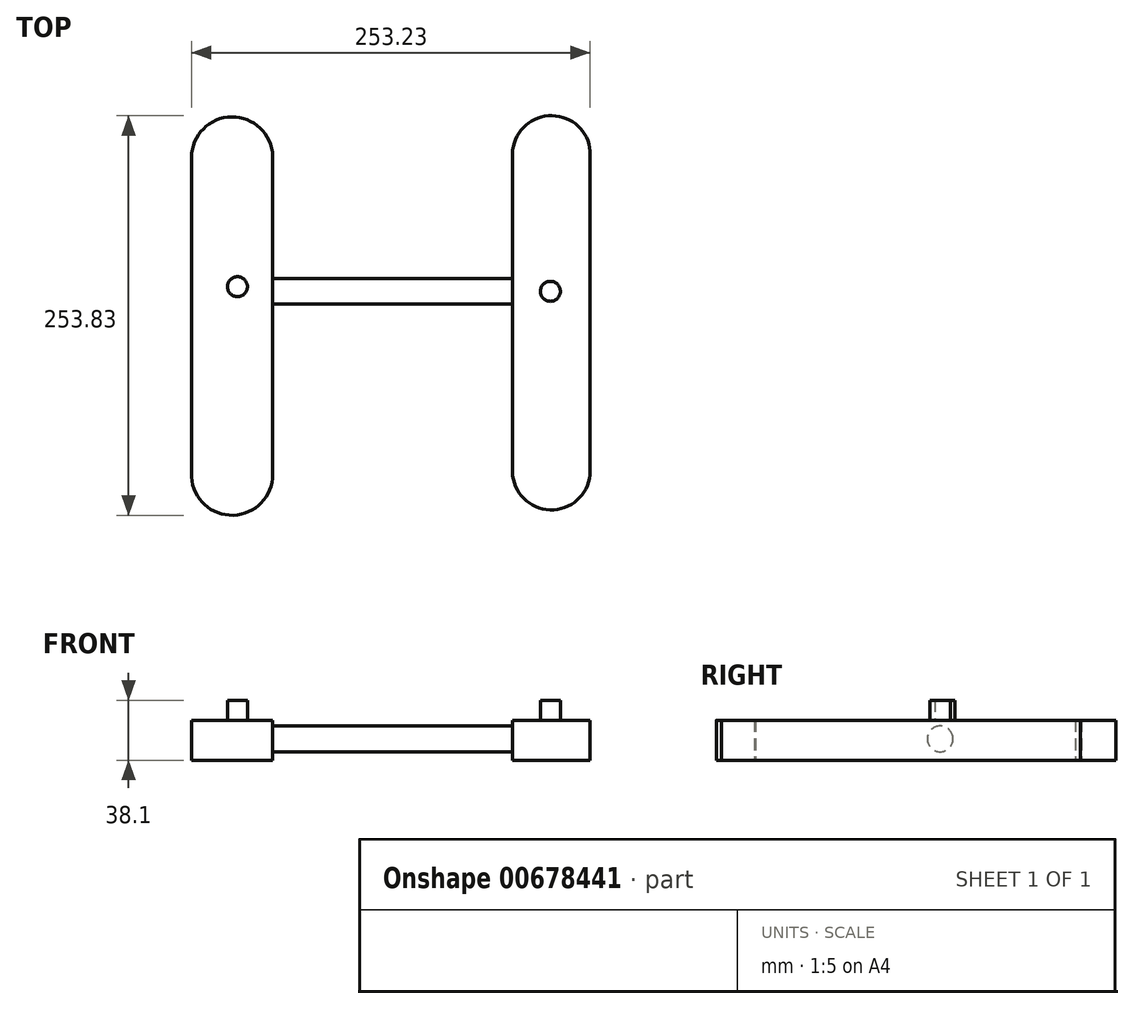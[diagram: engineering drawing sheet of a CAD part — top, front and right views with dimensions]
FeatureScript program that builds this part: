
annotation { "Feature Type Name" : "Feature", "Feature Type Description" : "" }
export const myFeature = defineFeature(function(context is Context, id is Id, definition is map)
    precondition{}
    {
        {
            var Q0;
            Q0=qCreatedBy(makeId("Top.planeOp"),FACE);
            var sketch = newSketch(context, id + "F0", { "sketchPlane" : qUnion([Q0])});
            skArc(sketch, "E0", {"start": v(-91.85, 86) * mm, "mid": v(-118.01, 110.82) * mm, "end": v(-143.42, 85.23) * mm});
            skLineSegment(sketch, "E1", {"start": v(-143.42, 85.23) * mm, "end": v(-143.42, -117.97) * mm});
            skLineSegment(sketch, "E2", {"start": v(-91.85, 86) * mm, "end": v(-91.85, -116.43) * mm});
            skArc(sketch, "E3", {"start": v(109.8, 89.08) * mm, "mid": v(85.52, 111.58) * mm, "end": v(60.55, 89.85) * mm});
            skLineSegment(sketch, "E4", {"start": v(60.55, 89.85) * mm, "end": v(60.55, -117.2) * mm});
            skLineSegment(sketch, "E5", {"start": v(109.8, 89.08) * mm, "end": v(109.8, -114.12) * mm});
            skArc(sketch, "E6", {"start": v(60.55, -117.2) * mm, "mid": v(86.62, -138.8) * mm, "end": v(109.8, -114.12) * mm});
            skArc(sketch, "E7", {"start": v(-143.42, -117.97) * mm, "mid": v(-116.9, -142.23) * mm, "end": v(-91.85, -116.43) * mm});
            skSolve(sketch);
        }
        {
            var Q0;
            Q0 = qSketchRegion(id + "F0", true);
            extrude(context, id + "F1", {"entities" : qUnion([Q0]), "depth" : 25.4 * mm, "offsetDistance" : 25.4 * mm});
        }
        {
            var Q0;
            Q0=makeQuery(id+"F1.opExtrude","SWEPT_FACE",FACE,{"disambiguationData":[OSD([sQuery(id+"F0.wireOp",EDGE,"E4")])]});
            var sketch = newSketch(context, id + "F2", { "sketchPlane" : qUnion([Q0])});
            skCircle(sketch, "E8", {"center": v(0, 13.55) * mm, "radius": 8.15 * mm});
            skSolve(sketch);
        }
        {
            var Q0;
            Q0 = qSketchRegion(id + "F2", true);
            extrude(context, id + "F3", {"entities" : qUnion([Q0]), "depth" : 152.4 * mm, "offsetDistance" : 25.4 * mm});
        }
        {
            var Q0;
            Q0=makeQuery(id+"F1.opExtrude","CAP_FACE",FACE,{"disambiguationData":[OSD([sQuery(id+"F0.wireOp",EDGE,"E0"),sQuery(id+"F0.wireOp",EDGE,"E1"),sQuery(id+"F0.wireOp",EDGE,"E2"),sQuery(id+"F0.wireOp",EDGE,"E7")])],"isStart":false});
            var sketch = newSketch(context, id + "F4", { "sketchPlane" : qUnion([Q0])});
            skCircle(sketch, "E9", {"center": v(-114.27, 2.93) * mm, "radius": 6.35 * mm});
            skCircle(sketch, "E10", {"center": v(84.5, 0) * mm, "radius": 6.35 * mm});
            skSolve(sketch);
        }
        {
            var Q0;
            Q0 = qSketchRegion(id + "F4", true);
            extrude(context, id + "F5", {"entities" : qUnion([Q0]), "depth" : 12.7 * mm, "offsetDistance" : 25.4 * mm});
        }
    });
